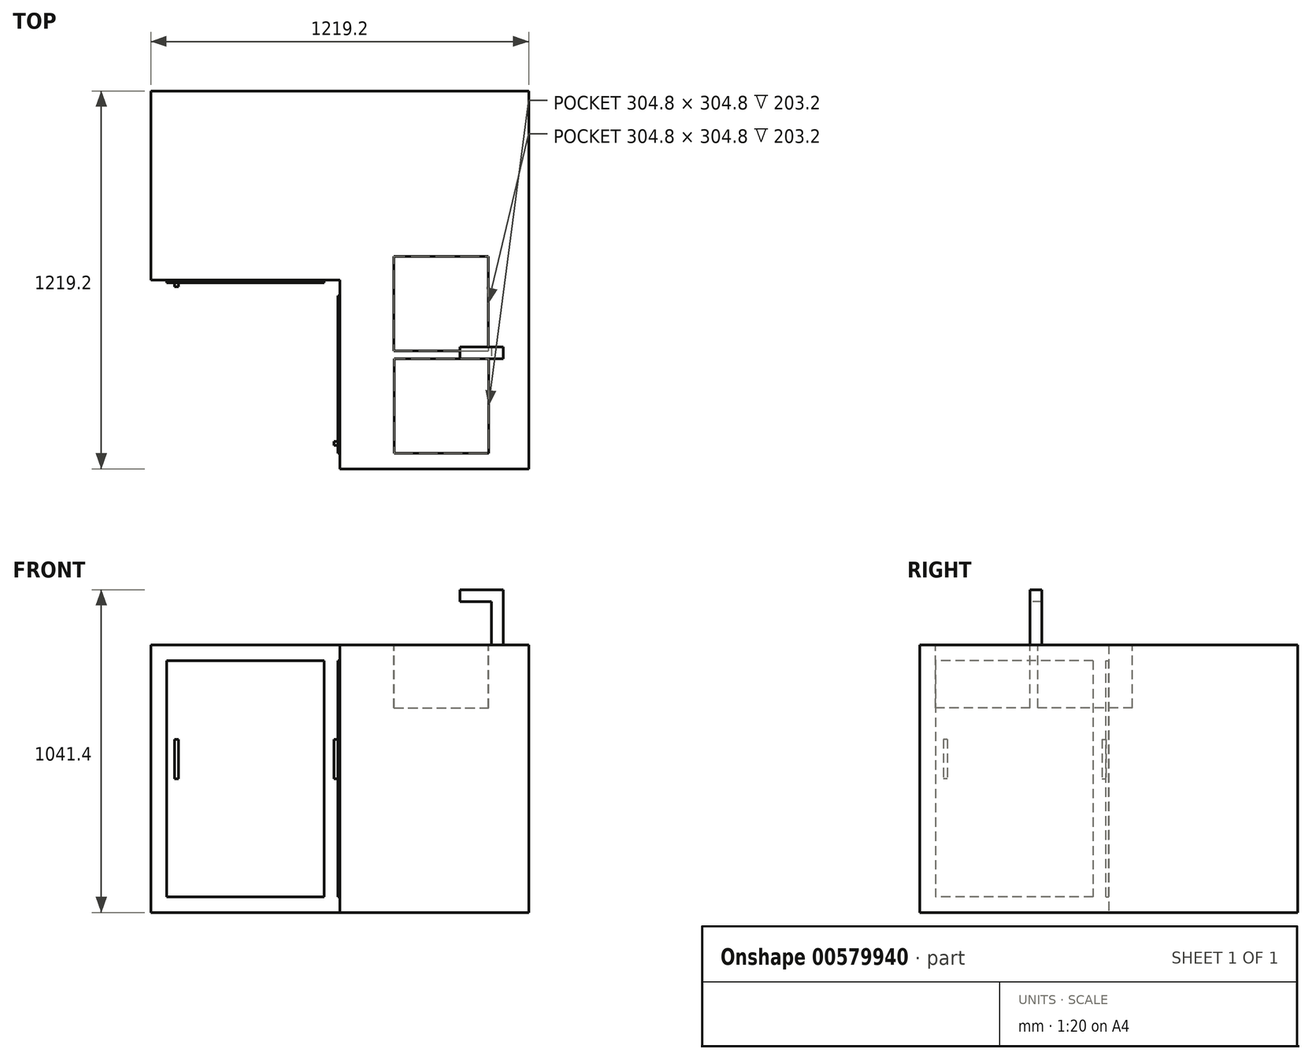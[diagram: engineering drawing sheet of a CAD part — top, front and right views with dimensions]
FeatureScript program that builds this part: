
annotation { "Feature Type Name" : "Feature", "Feature Type Description" : "" }
export const myFeature = defineFeature(function(context is Context, id is Id, definition is map)
    precondition{}
    {
        {
            var Q0;
            Q0=qCreatedBy(makeId("Front.planeOp"),FACE);
            var sketch = newSketch(context, id + "F0", { "sketchPlane" : qUnion([Q0])});
            skLineSegment(sketch, "E0.bottom", {"start": v(-238.74, 445.6) * mm, "end": v(370.86, 445.6) * mm});
            skLineSegment(sketch, "E0.top", {"start": v(-238.74, -418) * mm, "end": v(370.86, -418) * mm});
            skLineSegment(sketch, "E0.left", {"start": v(-238.74, 445.6) * mm, "end": v(-238.74, -418) * mm});
            skLineSegment(sketch, "E0.right", {"start": v(370.86, 445.6) * mm, "end": v(370.86, -418) * mm});
            skSolve(sketch);
        }
        {
            var Q0;
            Q0=makeQuery(id+"F0.imprint","IMPRINT",FACE,{"disambiguationData":[TD([[makeQuery(id+"F0.imprint","IMPRINT",EDGE,{"derivedFrom":sQuery(id+"F0.wireOp",EDGE,"E0.bottom")}),-1.0]])]});
            extrude(context, id + "F1", {"entities" : qUnion([Q0]), "depth" : 1219.2 * mm, "offsetDistance" : 25.4 * mm});
        }
        {
            var Q0;
            Q0=makeQuery(id+"F1.opExtrude","SWEPT_FACE",FACE,{"disambiguationData":[OSD([sQuery(id+"F0.wireOp",EDGE,"E0.left")])]});
            var sketch = newSketch(context, id + "F2", { "sketchPlane" : qUnion([Q0])});
            skLineSegment(sketch, "E1.bottom", {"start": v(0, 445.6) * mm, "end": v(609.6, 445.6) * mm});
            skLineSegment(sketch, "E1.top", {"start": v(0, -418) * mm, "end": v(609.6, -418) * mm});
            skLineSegment(sketch, "E1.left", {"start": v(0, 445.6) * mm, "end": v(0, -418) * mm});
            skLineSegment(sketch, "E1.right", {"start": v(609.6, 445.6) * mm, "end": v(609.6, -418) * mm});
            skSolve(sketch);
        }
        {
            var Q0;
            Q0=makeQuery(id+"F2.imprint","IMPRINT",FACE,{"disambiguationData":[TD([[makeQuery(id+"F2.imprint","IMPRINT",EDGE,{"derivedFrom":sQuery(id+"F2.wireOp",EDGE,"E1.bottom")}),1.0]])]});
            extrude(context, id + "F3", {"entities" : qUnion([Q0]), "operationType" : NewBodyOperationType.ADD, "depth" : 609.6 * mm, "offsetDistance" : 25.4 * mm});
        }
        {
            var Q0;
            Q0=makeQuery(id+"F1.opExtrude","SWEPT_FACE",FACE,{"disambiguationData":[OSD([sQuery(id+"F0.wireOp",EDGE,"E0.left")])]});
            var sketch = newSketch(context, id + "F4", { "sketchPlane" : qUnion([Q0])});
            skLineSegment(sketch, "E2.bottom", {"start": v(660.4, 394.8) * mm, "end": v(1168.4, 394.8) * mm});
            skLineSegment(sketch, "E2.top", {"start": v(660.4, -367.2) * mm, "end": v(1168.4, -367.2) * mm});
            skLineSegment(sketch, "E2.left", {"start": v(660.4, 394.8) * mm, "end": v(660.4, -367.2) * mm});
            skLineSegment(sketch, "E2.right", {"start": v(1168.4, 394.8) * mm, "end": v(1168.4, -367.2) * mm});
            skSolve(sketch);
        }
        {
            var Q0;
            Q0 = qSketchRegion(id + "F4", true);
            extrude(context, id + "F5", {"entities" : qUnion([Q0]), "operationType" : NewBodyOperationType.ADD, "depth" : 6.35 * mm, "offsetDistance" : 25.4 * mm});
        }
        {
            var Q0;
            Q0=makeQuery(id+"F3.opExtrude","SWEPT_FACE",FACE,{"disambiguationData":[OSD([sQuery(id+"F2.wireOp",EDGE,"E1.right")])]});
            var sketch = newSketch(context, id + "F6", { "sketchPlane" : qUnion([Q0])});
            skLineSegment(sketch, "E3.bottom", {"start": v(-797.54, -367.2) * mm, "end": v(-289.54, -367.2) * mm});
            skLineSegment(sketch, "E3.top", {"start": v(-797.54, 394.8) * mm, "end": v(-289.54, 394.8) * mm});
            skLineSegment(sketch, "E3.left", {"start": v(-797.54, -367.2) * mm, "end": v(-797.54, 394.8) * mm});
            skLineSegment(sketch, "E3.right", {"start": v(-289.54, -367.2) * mm, "end": v(-289.54, 394.8) * mm});
            skSolve(sketch);
        }
        {
            var Q0;
            Q0=makeQuery(id+"F6.imprint","IMPRINT",FACE,{"disambiguationData":[TD([[makeQuery(id+"F6.imprint","IMPRINT",EDGE,{"derivedFrom":sQuery(id+"F6.wireOp",EDGE,"E3.bottom")}),1.0]])]});
            extrude(context, id + "F7", {"entities" : qUnion([Q0]), "operationType" : NewBodyOperationType.ADD, "depth" : 8.9 * mm, "offsetDistance" : 25.4 * mm});
        }
        {
            var Q0;
            Q0=makeQuery(id+"F7.opExtrude","CAP_FACE",FACE,{"disambiguationData":[OSD([sQuery(id+"F6.wireOp",EDGE,"E3.bottom"),sQuery(id+"F6.wireOp",EDGE,"E3.top"),sQuery(id+"F6.wireOp",EDGE,"E3.left"),sQuery(id+"F6.wireOp",EDGE,"E3.right")])],"isStart":false});
            var sketch = newSketch(context, id + "F8", { "sketchPlane" : qUnion([Q0])});
            skLineSegment(sketch, "E4.bottom", {"start": v(-772.14, 140.8) * mm, "end": v(-759.44, 140.8) * mm});
            skLineSegment(sketch, "E4.top", {"start": v(-772.14, 13.8) * mm, "end": v(-759.44, 13.8) * mm});
            skLineSegment(sketch, "E4.left", {"start": v(-772.14, 140.8) * mm, "end": v(-772.14, 13.8) * mm});
            skLineSegment(sketch, "E4.right", {"start": v(-759.44, 140.8) * mm, "end": v(-759.44, 13.8) * mm});
            skSolve(sketch);
        }
        {
            var Q0;
            Q0=makeQuery(id+"F8.imprint","IMPRINT",FACE,{"disambiguationData":[TD([[makeQuery(id+"F8.imprint","IMPRINT",EDGE,{"derivedFrom":sQuery(id+"F8.wireOp",EDGE,"E4.bottom")}),-1.0]])]});
            extrude(context, id + "F9", {"entities" : qUnion([Q0]), "operationType" : NewBodyOperationType.ADD, "depth" : 12.7 * mm, "offsetDistance" : 25.4 * mm});
        }
        {
            var Q0;
            Q0=makeQuery(id+"F5.opExtrude","CAP_FACE",FACE,{"disambiguationData":[OSD([sQuery(id+"F4.wireOp",EDGE,"E2.bottom"),sQuery(id+"F4.wireOp",EDGE,"E2.top"),sQuery(id+"F4.wireOp",EDGE,"E2.left"),sQuery(id+"F4.wireOp",EDGE,"E2.right")])],"isStart":false});
            var sketch = newSketch(context, id + "F10", { "sketchPlane" : qUnion([Q0])});
            skLineSegment(sketch, "E5.bottom", {"start": v(1130.3, 140.8) * mm, "end": v(1143, 140.8) * mm});
            skLineSegment(sketch, "E5.top", {"start": v(1130.3, 13.8) * mm, "end": v(1143, 13.8) * mm});
            skLineSegment(sketch, "E5.left", {"start": v(1130.3, 140.8) * mm, "end": v(1130.3, 13.8) * mm});
            skLineSegment(sketch, "E5.right", {"start": v(1143, 140.8) * mm, "end": v(1143, 13.8) * mm});
            skSolve(sketch);
        }
        {
            var Q0;
            Q0=makeQuery(id+"F10.imprint","IMPRINT",FACE,{"disambiguationData":[TD([[makeQuery(id+"F10.imprint","IMPRINT",EDGE,{"derivedFrom":sQuery(id+"F10.wireOp",EDGE,"E5.bottom")}),-1.0]])]});
            extrude(context, id + "F11", {"entities" : qUnion([Q0]), "operationType" : NewBodyOperationType.ADD, "depth" : 12.7 * mm, "offsetDistance" : 25.4 * mm});
        }
        {
            var Q0;
            Q0=makeQuery(id+"F3.boolean.opBoolean","MERGE",FACE,{"derivedFrom":[makeQuery(id+"F1.opExtrude","SWEPT_FACE",FACE,{"disambiguationData":[OSD([sQuery(id+"F0.wireOp",EDGE,"E0.bottom")])]}),makeQuery(id+"F3.opExtrude","SWEPT_FACE",FACE,{"disambiguationData":[OSD([sQuery(id+"F2.wireOp",EDGE,"E1.bottom")])]})]});
            var sketch = newSketch(context, id + "F12", { "sketchPlane" : qUnion([Q0])});
            skLineSegment(sketch, "E6.bottom", {"start": v(-64.14, -533.4) * mm, "end": v(240.66, -533.4) * mm});
            skLineSegment(sketch, "E6.top", {"start": v(-64.14, -838.2) * mm, "end": v(240.66, -838.2) * mm});
            skLineSegment(sketch, "E6.left", {"start": v(-64.14, -533.4) * mm, "end": v(-64.14, -838.2) * mm});
            skLineSegment(sketch, "E6.right", {"start": v(240.66, -533.4) * mm, "end": v(240.66, -838.2) * mm});
            skLineSegment(sketch, "E7.bottom", {"start": v(-62.93, -863.6) * mm, "end": v(241.87, -863.6) * mm});
            skLineSegment(sketch, "E7.top", {"start": v(-62.93, -1168.4) * mm, "end": v(241.87, -1168.4) * mm});
            skLineSegment(sketch, "E7.left", {"start": v(-62.93, -863.6) * mm, "end": v(-62.93, -1168.4) * mm});
            skLineSegment(sketch, "E7.right", {"start": v(241.87, -863.6) * mm, "end": v(241.87, -1168.4) * mm});
            skSolve(sketch);
        }
        {
            var Q0;
            Q0=makeQuery(id+"F12.imprint","IMPRINT",FACE,{"disambiguationData":[TD([[makeQuery(id+"F12.imprint","IMPRINT",EDGE,{"derivedFrom":sQuery(id+"F12.wireOp",EDGE,"E6.bottom")}),-1.0]])]});
            var Q1;
            Q1=makeQuery(id+"F12.imprint","IMPRINT",FACE,{"disambiguationData":[TD([[makeQuery(id+"F12.imprint","IMPRINT",EDGE,{"derivedFrom":sQuery(id+"F12.wireOp",EDGE,"E7.bottom")}),-1.0]])]});
            extrude(context, id + "F13", {"entities" : qUnion([Q0, Q1]), "operationType" : NewBodyOperationType.REMOVE, "oppositeDirection" : true, "depth" : 203.2 * mm, "offsetDistance" : 25.4 * mm});
        }
        {
            var Q0;
            Q0=makeQuery(id+"F3.boolean.opBoolean","MERGE",FACE,{"derivedFrom":[makeQuery(id+"F1.opExtrude","SWEPT_FACE",FACE,{"disambiguationData":[OSD([sQuery(id+"F0.wireOp",EDGE,"E0.bottom")])]}),makeQuery(id+"F3.opExtrude","SWEPT_FACE",FACE,{"disambiguationData":[OSD([sQuery(id+"F2.wireOp",EDGE,"E1.bottom")])]})]});
            var sketch = newSketch(context, id + "F14", { "sketchPlane" : qUnion([Q0])});
            skLineSegment(sketch, "E8.bottom", {"start": v(250.27, -825.5) * mm, "end": v(288.37, -825.5) * mm});
            skLineSegment(sketch, "E8.top", {"start": v(250.27, -863.6) * mm, "end": v(288.37, -863.6) * mm});
            skLineSegment(sketch, "E8.left", {"start": v(250.27, -825.5) * mm, "end": v(250.27, -863.6) * mm});
            skLineSegment(sketch, "E8.right", {"start": v(288.37, -825.5) * mm, "end": v(288.37, -863.6) * mm});
            skSolve(sketch);
        }
        {
            var Q0;
            Q0 = qSketchRegion(id + "F14", true);
            extrude(context, id + "F15", {"entities" : qUnion([Q0]), "operationType" : NewBodyOperationType.ADD, "depth" : 177.8 * mm, "offsetDistance" : 25.4 * mm});
        }
        {
            var Q0;
            Q0=makeQuery(id+"F15.opExtrude","SWEPT_FACE",FACE,{"disambiguationData":[OSD([sQuery(id+"F14.wireOp",EDGE,"E8.left")])]});
            var sketch = newSketch(context, id + "F16", { "sketchPlane" : qUnion([Q0])});
            skLineSegment(sketch, "E9.bottom", {"start": v(825.5, 623.4) * mm, "end": v(863.6, 623.4) * mm});
            skLineSegment(sketch, "E9.top", {"start": v(825.5, 585.3) * mm, "end": v(863.6, 585.3) * mm});
            skLineSegment(sketch, "E9.left", {"start": v(825.5, 623.4) * mm, "end": v(825.5, 585.3) * mm});
            skLineSegment(sketch, "E9.right", {"start": v(863.6, 623.4) * mm, "end": v(863.6, 585.3) * mm});
            skSolve(sketch);
        }
        {
            var Q0;
            Q0=makeQuery(id+"F16.imprint","IMPRINT",FACE,{"disambiguationData":[TD([[makeQuery(id+"F16.imprint","IMPRINT",EDGE,{"derivedFrom":sQuery(id+"F16.wireOp",EDGE,"E9.bottom")}),-1.0]])]});
            extrude(context, id + "F17", {"entities" : qUnion([Q0]), "operationType" : NewBodyOperationType.ADD, "depth" : 101.6 * mm, "offsetDistance" : 25.4 * mm});
        }
    });
